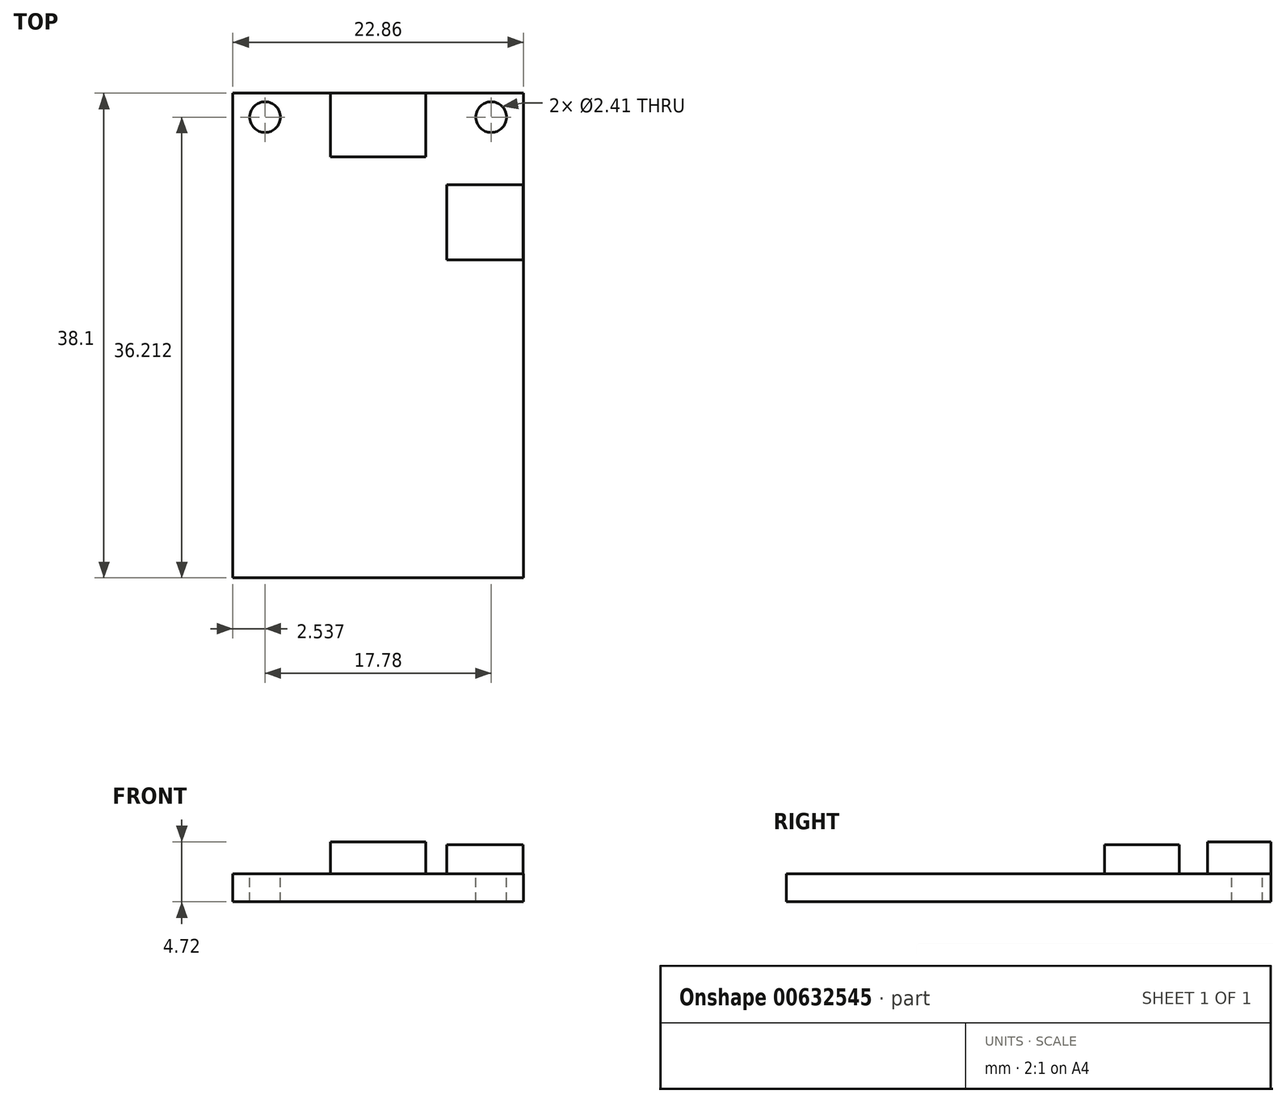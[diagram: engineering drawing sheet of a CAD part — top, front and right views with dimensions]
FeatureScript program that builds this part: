
annotation { "Feature Type Name" : "Feature", "Feature Type Description" : "" }
export const myFeature = defineFeature(function(context is Context, id is Id, definition is map)
    precondition{}
    {
        {
            var Q0;
            Q0=qCreatedBy(makeId("Top.planeOp"),FACE);
            var sketch = newSketch(context, id + "F0", { "sketchPlane" : qUnion([Q0])});
            skLineSegment(sketch, "E0.bottom", {"start": v(-41.42, 22.67) * mm, "end": v(-18.56, 22.67) * mm});
            skLineSegment(sketch, "E0.top", {"start": v(-41.42, -15.43) * mm, "end": v(-18.56, -15.43) * mm});
            skLineSegment(sketch, "E0.left", {"start": v(-41.42, 22.67) * mm, "end": v(-41.42, -15.43) * mm});
            skLineSegment(sketch, "E0.right", {"start": v(-18.56, 22.67) * mm, "end": v(-18.56, -15.43) * mm});
            skSolve(sketch);
        }
        {
            var Q0;
            Q0=makeQuery(id+"F0.imprint","IMPRINT",FACE,{"disambiguationData":[TD([[makeQuery(id+"F0.imprint","IMPRINT",EDGE,{"derivedFrom":sQuery(id+"F0.wireOp",EDGE,"E0.bottom")}),-1.0]])]});
            extrude(context, id + "F1", {"entities" : qUnion([Q0]), "depth" : 4.5 * mm, "offsetDistance" : 25.4 * mm});
        }
        {
            var Q0;
            Q0=makeQuery(id+"F1.opExtrude","CAP_FACE",FACE,{"disambiguationData":[OSD([sQuery(id+"F0.wireOp",EDGE,"E0.bottom"),sQuery(id+"F0.wireOp",EDGE,"E0.top"),sQuery(id+"F0.wireOp",EDGE,"E0.left"),sQuery(id+"F0.wireOp",EDGE,"E0.right")])],"isStart":false});
            var sketch = newSketch(context, id + "F2", { "sketchPlane" : qUnion([Q0])});
            skLineSegment(sketch, "E1.bottom", {"start": v(-24.61, 15.46) * mm, "end": v(-18.61, 15.46) * mm});
            skLineSegment(sketch, "E1.top", {"start": v(-24.61, 9.56) * mm, "end": v(-18.61, 9.56) * mm});
            skLineSegment(sketch, "E1.left", {"start": v(-24.61, 15.46) * mm, "end": v(-24.61, 9.56) * mm});
            skLineSegment(sketch, "E1.right", {"start": v(-18.61, 15.46) * mm, "end": v(-18.61, 9.56) * mm});
            skPoint(sketch, "E1.middle", {"position": v(-21.61, 12.5) * mm});
            skSolve(sketch);
        }
        {
            var Q0;
            Q0=makeQuery(id+"F2.imprint","IMPRINT",FACE,{"disambiguationData":[TD([[makeQuery(id+"F2.imprint","IMPRINT",EDGE,{"derivedFrom":sQuery(id+"F2.wireOp",EDGE,"E1.bottom")}),1.0]])]});
            extrude(context, id + "F3", {"entities" : qUnion([Q0]), "operationType" : NewBodyOperationType.REMOVE, "oppositeDirection" : true, "depth" : 2.3 * mm, "offsetDistance" : 25.4 * mm});
        }
        {
            var Q0;
            Q0=makeQuery(id+"F3.boolean.opBoolean","COPY",FACE,{"derivedFrom":makeQuery(id+"F3.opExtrude","CAP_FACE",FACE,{"disambiguationData":[OSD([sQuery(id+"F0.wireOp",EDGE,"E0.bottom"),sQuery(id+"F0.wireOp",EDGE,"E0.top"),sQuery(id+"F0.wireOp",EDGE,"E0.left"),sQuery(id+"F0.wireOp",EDGE,"E0.right"),sQuery(id+"F2.wireOp",EDGE,"EEPtLPqM-pRcE-5c5X-eBK0-mj0rIQGNl9eK.bottom"),sQuery(id+"F2.wireOp",EDGE,"EEPtLPqM-pRcE-5c5X-eBK0-mj0rIQGNl9eK.top"),sQuery(id+"F2.wireOp",EDGE,"EEPtLPqM-pRcE-5c5X-eBK0-mj0rIQGNl9eK.left")])],"isStart":false})});
            var sketch = newSketch(context, id + "F4", { "sketchPlane" : qUnion([Q0])});
            skLineSegment(sketch, "E2.bottom", {"start": v(-26.24, 17.67) * mm, "end": v(-33.74, 17.67) * mm});
            skLineSegment(sketch, "E2.top", {"start": v(-26.24, 22.67) * mm, "end": v(-33.74, 22.67) * mm});
            skLineSegment(sketch, "E2.left", {"start": v(-26.24, 17.67) * mm, "end": v(-26.24, 22.67) * mm});
            skLineSegment(sketch, "E2.right", {"start": v(-33.74, 17.67) * mm, "end": v(-33.74, 22.67) * mm});
            skPoint(sketch, "E2.middle", {"position": v(-29.99, 20.17) * mm});
            skSolve(sketch);
        }
        {
            var Q0;
            Q0 = qSketchRegion(id + "F4", true);
            extrude(context, id + "F5", {"entities" : qUnion([Q0]), "operationType" : NewBodyOperationType.ADD, "depth" : 2.5 * mm, "offsetDistance" : 25.4 * mm});
        }
        {
            var Q0;
            Q0=makeQuery(id+"F3.boolean.opBoolean","COPY",FACE,{"derivedFrom":makeQuery(id+"F3.opExtrude","CAP_FACE",FACE,{"disambiguationData":[OSD([sQuery(id+"F0.wireOp",EDGE,"E0.bottom"),sQuery(id+"F0.wireOp",EDGE,"E0.top"),sQuery(id+"F0.wireOp",EDGE,"E0.left"),sQuery(id+"F0.wireOp",EDGE,"E0.right"),sQuery(id+"F2.wireOp",EDGE,"E1.bottom"),sQuery(id+"F2.wireOp",EDGE,"E1.top"),sQuery(id+"F2.wireOp",EDGE,"E1.left"),sQuery(id+"F2.wireOp",EDGE,"E1.right")])],"isStart":false})});
            var sketch = newSketch(context, id + "F6", { "sketchPlane" : qUnion([Q0])});
            skPoint(sketch, "E3", {"position": v(-38.88, 20.78) * mm});
            skPoint(sketch, "E4", {"position": v(-21.1, 20.78) * mm});
            skSolve(sketch);
        }
        {
            var Q0;
            Q0=sQuery(id+"F6.wireOp",VERTEX,"E3");
            var Q1;
            Q1=sQuery(id+"F6.wireOp",VERTEX,"E4");
            var Q2;
            Q2=makeQuery(id+"F1.opExtrude","SWEPT_BODY",BODY,{"disambiguationData":[OSD([sQuery(id+"F0.wireOp",EDGE,"E0.bottom"),sQuery(id+"F0.wireOp",EDGE,"E0.top"),sQuery(id+"F0.wireOp",EDGE,"E0.left"),sQuery(id+"F0.wireOp",EDGE,"E0.right")])]});
            hole(context, id + "F7", {"style" : HoleStyle.SIMPLE, "endStyle" : HoleEndStyle.THROUGH, "holeDiameter" : 2.41 * mm, "majorDiameter" : 6.35 * mm, "isTappedThrough" : true, "tappedDepth" : 12.7 * mm, "tapClearance" : 3, "locations" : qUnion([Q0, Q1]), "scope" : qUnion([Q2])});
        }
    });
